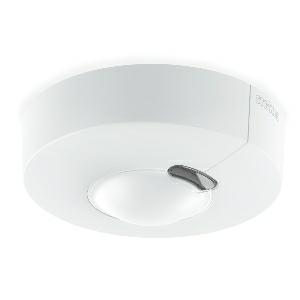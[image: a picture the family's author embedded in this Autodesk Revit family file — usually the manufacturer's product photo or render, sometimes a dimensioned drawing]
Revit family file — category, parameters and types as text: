
# Revit family: hf_3360_033668
name_source: partatom
category: Elektroinstallationen
revit_build: Autodesk Revit 2016 (Build: 20190508_0715(x64)
units: mm (PartAtom-declared; Revit-internal decimal feet)

## family parameters
Basisbauteil = Fläche
Beim Laden mit Abzugskörper schneiden = Nein
Bemaßung runder Anschluss = Durchmesser verwenden
Beschriftungsausrichtung beibehalten = Nein
Gemeinsam genutzt = Nein
Raumberechnungspunkt = Nein
Teiletyp = Normal

## types (1)
- HF 3360
    Apparent Load = 0 VA
    Beschreibung = Type: Motion detectors; Dimensions (Ø x H): 126 x 52 mm; Mains power supply: 220 – 240 V / 50 – 60 Hz; Sensor Technology: High frequency; Application, place: Indoors; Application, room: function room / ancillary room, stairwell, WC / washroom, multi-storey / underground car park, Indoors; Installation site: wall, ceiling, corner; Installation: Surface wiring; HF-system: 5,8 GHz; Electronic scalability: Yes; Mechanical scalability: No; Mounting height: 2,00 – 4,00 m; Optimum mounting height: 2,8 m; Detection: also through glass, wood and stud walls; Detection angle: 360 °; Angle of aperture: 140 °; Sneak-by guard: Yes; Reach, radial: Ø 8 m (50 m²); Reach, tangential: Ø 8 m (50 m²); Twilight setting TEACH: Yes; Twilight setting: 2 – 1000 lx; Time setting: 5 sec – 15 min; Switching output 1, resistive: 2000 W; Switching output 1, number of LEDs / fluorescent lamps: 8 pcs.; Constant-lighting control: No; Basic light level function: No; Functions: Normal / test mode, Manual ON / ON-OFF; Settings via: Remote control, Potentiometers, Smart Remote; With remote control: No; Interconnection: Yes; IP-rating: IP54; Material: Plastic; Ambient temperature: -20 – 50 °C; Colour: white; Colour, RAL: 9003; Manufacturer's Warranty: 5 years; Version: COM1 - surface, rd.; PU1, EAN: 4007841033668
    Height = 0 mm  [stored 0 ft]
    Hersteller = Steinel
    Length = 126 mm
    ModVariant = Nein
    Modell = 033668
    Mounting Type = Surface mounted
    Number of Poles = 1
    OnlyDefault = Ja
    Power Factor = 1
    Product Name = HF 3360
    Product group = Sensor-switched indoor light
    ProductGroupID = 30
    Protection Class = Protection class
    Protection Degree = IP 54
    RlxData = <blob elided: 37605 chars, md5=9e34699d>
    SensorDataFile = {"IESDataFiles":[]}
    Typenbild = produkt1_033668.jpg
    Typenkommentare = Product without accessories
    URL = http://relux.com
    VarID = ---
    Voltage = 0 V
    Vorgabe-Ansicht = 1800 mm
    Weight = 0.00 kg
    Width = 0 mm  [stored 0 ft]

note: [stored X ft] marks values corroborated as IEEE doubles in the binary element streams (Revit-internal decimal feet)

## geometry (parser evidence)
native form markers: Sweep x12
no freeform markers — native parametric forms only
